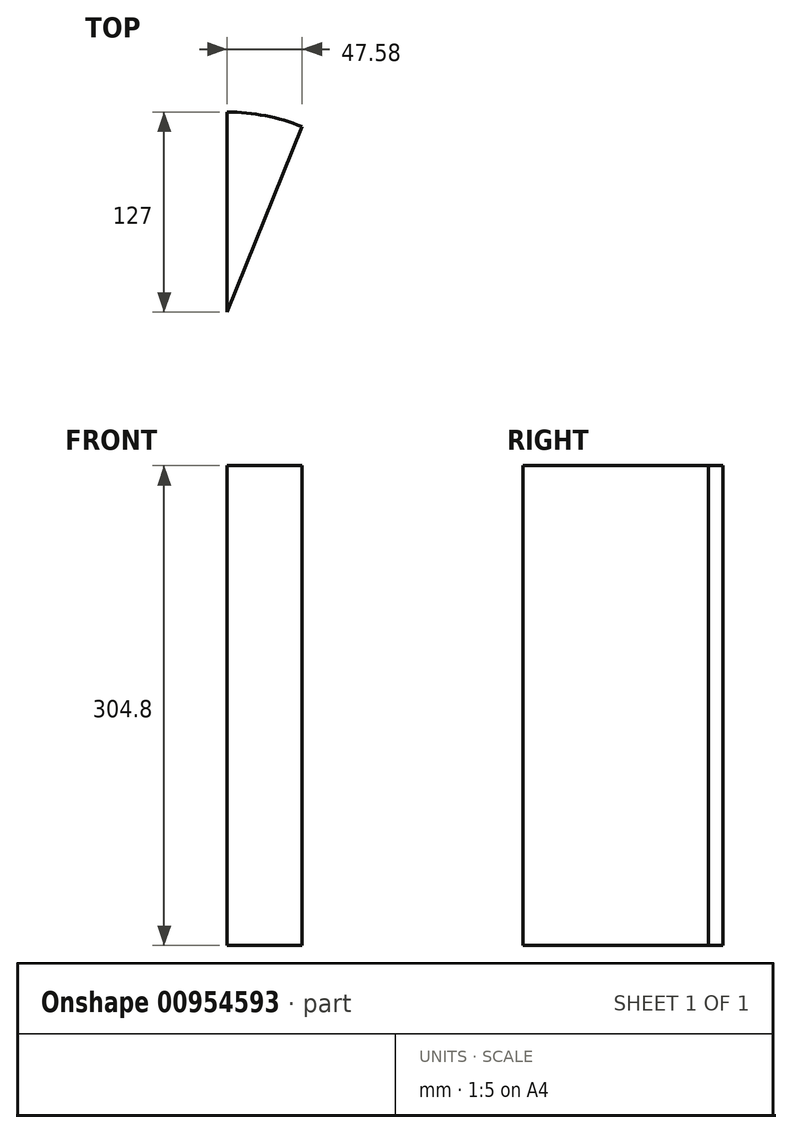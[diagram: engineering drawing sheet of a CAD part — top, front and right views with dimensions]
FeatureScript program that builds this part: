
annotation { "Feature Type Name" : "Feature", "Feature Type Description" : "" }
export const myFeature = defineFeature(function(context is Context, id is Id, definition is map)
    precondition{}
    {
        {
            var Q0;
            Q0=qCreatedBy(makeId("Top.planeOp"),FACE);
            var sketch = newSketch(context, id + "F0", { "sketchPlane" : qUnion([Q0])});
            skCircle(sketch, "E0", {"center": v(0, 0) * mm, "radius": 127 * mm});
            skSolve(sketch);
        }
        {
            var Q0;
            Q0=qCreatedBy(makeId("Top.planeOp"),FACE);
            var sketch = newSketch(context, id + "F1", { "sketchPlane" : qUnion([Q0])});
            skLineSegment(sketch, "E1", {"start": v(0, 0) * mm, "end": v(0, 127) * mm});
            skLineSegment(sketch, "E2", {"start": v(47.58, 117.75) * mm, "end": v(0, 0) * mm});
            skArc(sketch, "E3.0", {"start": v(47.58, 117.75) * mm, "mid": v(24.23, 124.67) * mm, "end": v(0, 127) * mm});
            skSolve(sketch);
        }
        {
            var Q0;
            Q0 = qSketchRegion(id + "F1", true);
            var Q1;
            Q1=makeQuery(id+"F1.imprint","IMPRINT",FACE,{"disambiguationData":[TD([[makeQuery(id+"F1.imprint","IMPRINT",EDGE,{"derivedFrom":sQuery(id+"F1.wireOp",EDGE,"E1")}),-1.0]])]});
            extrude(context, id + "F2", {"entities" : qUnion([Q0, Q1]), "depth" : 304.8 * mm, "offsetDistance" : 25.4 * mm});
        }
    });
